# Revit family: SUPER_MAX-OS
name_source: partatom
category: Plumbing Fixtures
units: mm (PartAtom-declared; Revit-internal decimal feet)

## family parameters
Always vertical = Yes
Cut with Voids When Loaded = No
OmniClass Number = 23.45.00.00
OmniClass Title = Sanitary, Laundry, and Cleaning Equipment
Part Type = Normal
Room Calculation Point = No
Round Connector Dimension = Use Diameter
Shared = No
Work Plane-Based = No

## types (6) — shared parameters
A = 111"
B = 64"
Base material = Default
Manufacturer = MIFAB
Material = Polyethylene, High Density
URL = www.mifab.com

## per-type parameters (varying)
| type | D | Description | E | Model | a |
| SUPER-500OS | 24 1/4" | 500gallon Super Max Liquid Hold Cap. Gravity Oil/Sediment interceptor | 40 1/2" | SM-MI-G-PL-500 | 8" |
| SUPER-750OS | 32 7/8" | 750gallon Super Max Liquid Hold Cap. Gravity Oil/Sediment interceptor | 49 1/8" | SM-MI-G-PL-750 | 13" |
| SUPER-1000OS | 43 1/4" | 1000gallon Super Max Liquid Hold Cap. Gravity Oil/Sediment interceptor | 59 1/2" | SM-MI-G-PL-1000 | 0" |
| SUPER-1300OS | 54 1/4" | 1300gallon Super Max Liquid Hold Cap. Gravity Oil/Sediment interceptor | 70 1/2" | SM-MI-G-PL-1300 | 0" |
| SUPER-1500OS | 62" | 1500gallon Super Max Liquid Hold Cap. Gravity Oil/Sediment interceptor | 78 1/4" | SM-MI-G-PL-1500 | 0" |
| SUPER-2000OS | 83 1/2" | 2000gallon Super Max Liquid Hold Cap. Gravity Oil/Sediment interceptor | 99 3/4" | SM-MI-G-PL-2000 | 0" |

## geometry (parser evidence)
native form markers: Sweep x3
no freeform markers — native parametric forms only
